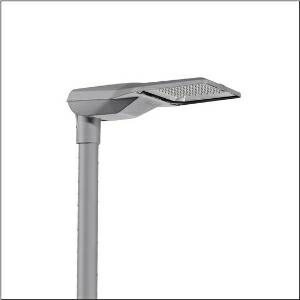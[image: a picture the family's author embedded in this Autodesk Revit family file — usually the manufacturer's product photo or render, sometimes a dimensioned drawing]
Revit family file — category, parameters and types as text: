
# Revit family: streetlight_sl_21_iq_midi___st0_8a_5xe3c31d08nb_f3e6
name_source: partatom
category: Lighting Fixtures
units: mm (PartAtom-declared; Revit-internal decimal feet)

## family parameters
Cut with Voids When Loaded = No
Host = Face
Light Source = No
Part Type = Normal
Room Calculation Point = No
Round Connector Dimension = Use Diameter
Shared = No

## types (1)
- --- (1 x LED, 23230 lm, 155.5 W, 3000K)
    Apparent Load = 155 VA
    CIE Flux Codes = 41 75 97 100 100
    Color Rendering = 70
    Color Temperature = 3000K
    Default Elevation = 1800 mm
    Description = Streetlight SL 21 iQ midi, mast luminaire, primary light control with lens, of PMMA, primary optical cover: cover, of toughened safety glass, transparent, light distribution: ST0.8a, light emission: direct distribution, primary light characteristic: asymmetric, installation type: post-top, side-entry, LED, High Power LED, rated luminous flux: 23.230lm, luminous efficacy: 149lm/W, light colour: 730, colour temperature: 3000K, control gear: iQ-Comfort, control: Auto-Match, Temp-Guard, Lumen-Switch, Night-Set, Smart-Wire, Light-Fading, Desk-Remote (wireless, voltage-free reading and setting of iQ features in the workshop via application-optimized NFC function/RFID function), optimised constant luminous flux control (CLO 2.0), pre-setting: linear dimming characteristic, mains connection: 230..240V, AC, 50/60Hz, start of lifetime: 156W, end of service life: 162W, reduction: 69W, luminaire housing, of diecast aluminium, powder-coated, SITECO metallic grey (DB 702S), corrosivity category C5 high according to DIN EN ISO 12944, please order mast flange separately, inclination adjustable: 0°, 5°, 10°, 15°, sealing non-destructively replaceable, multi-level sealing system, length: 644mm, width: 335mm, height: 110mm, mast flange for spigot size: 42mm (side-entry): 5XC10008XM4, 60/48mm (side-entry/post-top): 5XC10108XM2, 76/60mm (side-entry/post-top): 5XC10108XM1, mounting height: 4..8m, protection rating (complete): IP66, insulation class (complete): insulation class II (safety insulation), certification: CE, ENEC, ENEC+, VDE, impact resistance: IK10, permissible operating ambient temperature for outdoor applications: -40..+50°C, standard-compliant lighting for roads and squares, packaging unit: 1 piece

Light Distribution: ST0.8a
    Height = 111 mm
    Lamp = 1 x LED
    Lamp Light Flux = 23230 lm
    Lamp Power = 155.5 W
    Lamp count = 1
    Length = 644 mm
    Luminous efficacy = 149 lm/W
    Manufacturer = Siteco
    ModVariant = No
    Model = 5XE3C31D08NB
    Number of Poles = 1
    OnlyDefault = Yes
    Power Factor = 1
    Product Name = Streetlight SL 21 iQ midi | ST0.8a
    Product group = mast luminaire | pylon top
    ProductGroupID = 6100
    Protection Class = Protection class II
    Protection Degree = IP 66
    RLX_Detail_Level = 1
    RLX_Emergency_Light_Flux = 0 lm
    RLX_Emergency_Type = 0
    RLX_Emergency_Type_DB = No
    RlxData = <blob elided: 27241 chars, md5=a1d7e7d3>
    Socket = socket
    Standby Power = 0 W
    System Light Flux = 23230 lm
    System Power = 155 W
    Type Comments = factory setting: luminous flux: 100 % | dim-lin: 254 | 823 mA
    Type Image = l_1004298.jpg
    URL = http://relux.com
    VarID = @adj_168473
    Voltage = 0 V
    Weight = 0.00 kg
    Width = 336 mm

## geometry (parser evidence)
native form markers: Blend x4, Sweep x13
no freeform markers — native parametric forms only
